# Revit family: vazon_fort
name_source: partatom
category: Антураж
revit_build: Autodesk Revit 2017 (Build: 20160225_1515(x64)
units: mm (PartAtom-declared; Revit-internal decimal feet)

## family parameters
Всегда вертикально = Да
Источник визуального образа = Геометрия семейства
На основе рабочей плоскости = Нет
Общий = Нет
При загрузке вырезать с полостями = Нет
Точка расчета площади = Нет

## types (7) — shared parameters
Высота = 400 мм
Длина = 400 мм
Наименование = Вазон "Форт"
Объем бетона = 0.04 м³
Производитель = ГК Очаковский комбинат ЖБИ
Ширина = 600 мм

## per-type parameters (varying)
| type | URL | Материал |
| "Форт" Московский гравий |  | Очаковский_Московский_гравий |
| "Форт" Белый шелк |  | Очаковский_Белый_Шелк |
| "Форт" Черный глянец |  | Очаковский_Черный_глянец |
| "Форт" Черный шелк |  | Очаковский_Черный_шелк |
| "Форт" Шахматка |  | Очаковский_Шахматка |
| "Форт" Морская соль |  | Очаковский_Морская_соль |
| "Форт" Крымский берег | http://file-system.ru | Очаковский_Крымский_берег |

## geometry (parser evidence)
native form markers: Blend x149
no freeform markers — native parametric forms only
